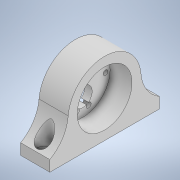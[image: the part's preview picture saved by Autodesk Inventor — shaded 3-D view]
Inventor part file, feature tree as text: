
AUTODESK INVENTOR PART (.ipt)
format: ipt  version: 2020 (Build 240168000, 168)  size: 216,064 bytes
history: native  units: in
note: dims shown in document units (in); Inventor stores cm internally (conversion verified against a paired STEP export)
features: sketch x6, extrude x5, fillet x2, hole x1
ambient origin geometry x8: Origin, YZ Plane, XZ Plane, XY Plane, X Axis, Y Axis, Z Axis, Center Point
bodies: Solid1 (feature_tree)
feature tree (14):
  extrude  "Extrusion1"  Depth=3.0in
  extrude  "Extrusion2"  Depth=0.5in
  extrude  "Extrusion3"  Depth=1.0in
  fillet  "Fillet1"  Radius=1.7in
  sketch  "Sketch6"  dims[d10=1.5in d11=0.6in d12=0.0in]
  fillet  "Fillet2"  Radius=1.0in
  hole  "Hole1"  [1 undecoded]
  extrude  "Extrusion5"  Depth=1.0in
  extrude  "Extrusion7"  Depth=1.0in
  sketch  "Sketch1"  dims[d0=0.8in d1=3.0in]
  sketch  "Sketch2"  dims[d2=0.3in d3=0.0in d4=0.5in]
  sketch  "Sketch3"  dims[d5=0.8in d6=2.0in d7=1.7in d8=0.0in d9=1.0in]
  sketch  "Sketch7"  dims[d19=1.0in d20=0.25in]
  sketch  "Sketch9"  dims[d21=0.25in d22=1.0in d23=0.2in d24=0.75in d25=0.4in d26=0.15in d27=0.5635in d28=1.0in d29=0.8108in d30=0.4in d31=0.4in d32=0.6in d33=0.0in d47=0.26in d48=120.0deg d49=60.0deg d50=0.06in d51=0.06in d52=60.0deg d53=0.14in d54=0.14in d55=0.06in d56=0.065in d57=0.06in d58=0.065in d59=0.06in d60=0.065in d61=0.06in d62=0.065in d63=1.0in d64=0.0in]
note: 1 required parameter value undecoded (feature->parameter linkage not recoverable at this tier; creation-order binding heuristic only, values carry confidence <= 0.55)
